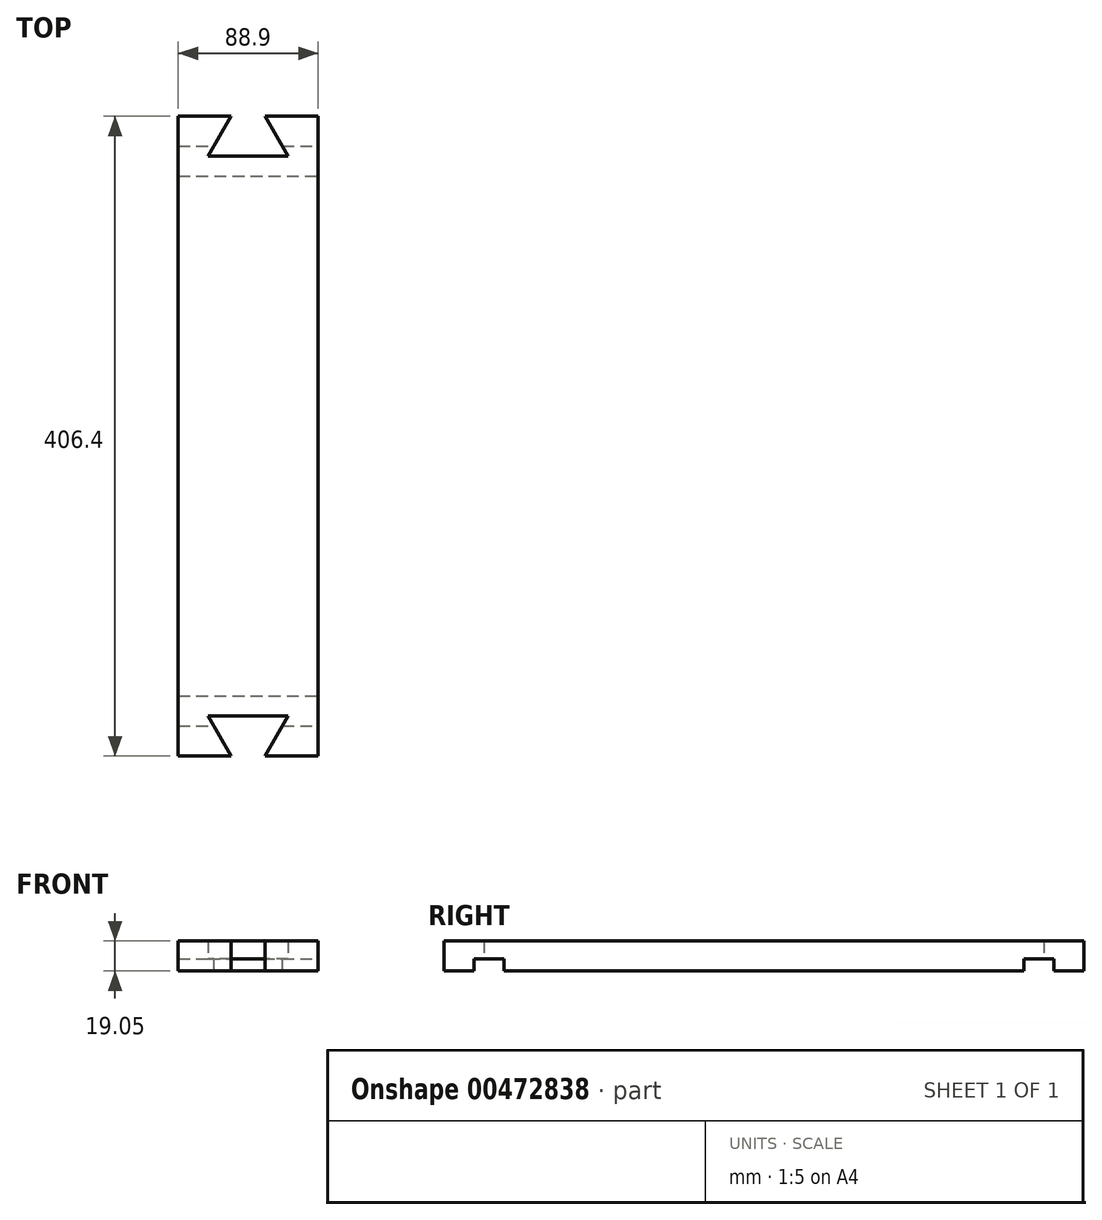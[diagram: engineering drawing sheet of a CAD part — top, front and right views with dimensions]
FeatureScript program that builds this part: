
annotation { "Feature Type Name" : "Feature", "Feature Type Description" : "" }
export const myFeature = defineFeature(function(context is Context, id is Id, definition is map)
    precondition{}
    {
        {
            var Q0;
            Q0=qCreatedBy(makeId("Top.planeOp"),FACE);
            var sketch = newSketch(context, id + "F0", { "sketchPlane" : qUnion([Q0])});
            skLineSegment(sketch, "E0.bottom", {"start": v(44.45, 203.2) * mm, "end": v(10.74, 203.2) * mm});
            skLineSegment(sketch, "E0.top", {"start": v(44.45, -203.2) * mm, "end": v(10.74, -203.2) * mm});
            skLineSegment(sketch, "E0.left", {"start": v(44.45, 203.2) * mm, "end": v(44.45, -203.2) * mm});
            skLineSegment(sketch, "E0.right", {"start": v(-44.45, 203.2) * mm, "end": v(-44.45, -203.2) * mm});
            skPoint(sketch, "E0.middle", {"position": v(0, 0) * mm});
            skLineSegment(sketch, "E1", {"start": v(-25.4, 177.8) * mm, "end": v(25.4, 177.8) * mm});
            skLineSegment(sketch, "E2", {"start": v(-25.4, 177.8) * mm, "end": v(-10.74, 203.2) * mm});
            skLineSegment(sketch, "E3", {"start": v(25.4, 177.8) * mm, "end": v(10.74, 203.2) * mm});
            skLineSegment(sketch, "E4.trimOffspring", {"start": v(-10.74, 203.2) * mm, "end": v(-44.45, 203.2) * mm});
            skLineSegment(sketch, "E5.MirrorCS", {"start": v(-10.74, -203.2) * mm, "end": v(-44.45, -203.2) * mm});
            skLineSegment(sketch, "E6.MirrorCS", {"start": v(25.4, -177.8) * mm, "end": v(10.74, -203.2) * mm});
            skLineSegment(sketch, "E7.MirrorCS", {"start": v(-25.4, -177.8) * mm, "end": v(-10.74, -203.2) * mm});
            skLineSegment(sketch, "E8.MirrorCS", {"start": v(-25.4, -177.8) * mm, "end": v(25.4, -177.8) * mm});
            skSolve(sketch);
        }
        {
            var Q0;
            Q0 = qSketchRegion(id + "F0", true);
            extrude(context, id + "F1", {"entities" : qUnion([Q0]), "depth" : 19.05 * mm});
        }
        {
            var Q0;
            Q0=makeQuery(id+"F1.opExtrude","SWEPT_FACE",FACE,{"disambiguationData":[OSD([sQuery(id+"F0.wireOp",EDGE,"E0.left")])]});
            var sketch = newSketch(context, id + "F2", { "sketchPlane" : qUnion([Q0])});
            skLineSegment(sketch, "E9.bottom", {"start": v(-184.15, 0) * mm, "end": v(-165.1, 0) * mm});
            skLineSegment(sketch, "E9.top", {"start": v(-184.15, 7.62) * mm, "end": v(-165.1, 7.62) * mm});
            skLineSegment(sketch, "E9.left", {"start": v(-184.15, 0) * mm, "end": v(-184.15, 7.62) * mm});
            skLineSegment(sketch, "E9.right", {"start": v(-165.1, 0) * mm, "end": v(-165.1, 7.62) * mm});
            skLineSegment(sketch, "E10.MirrorCS", {"start": v(165.1, 0) * mm, "end": v(165.1, 7.62) * mm});
            skLineSegment(sketch, "E11.MirrorCS", {"start": v(184.15, 0) * mm, "end": v(184.15, 7.62) * mm});
            skLineSegment(sketch, "E12.MirrorCS", {"start": v(184.15, 7.62) * mm, "end": v(165.1, 7.62) * mm});
            skLineSegment(sketch, "E13.MirrorCS", {"start": v(184.15, 0) * mm, "end": v(165.1, 0) * mm});
            skPoint(sketch, "E14.middle", {"position": v(0, 3.81) * mm});
            skSolve(sketch);
        }
        {
            var Q0;
            Q0 = qSketchRegion(id + "F2", true);
            extrude(context, id + "F3", {"entities" : qUnion([Q0]), "operationType" : NewBodyOperationType.REMOVE, "endBound" : BoundingType.THROUGH_ALL, "oppositeDirection" : true, "depth" : 25.4 * mm});
        }
    });
